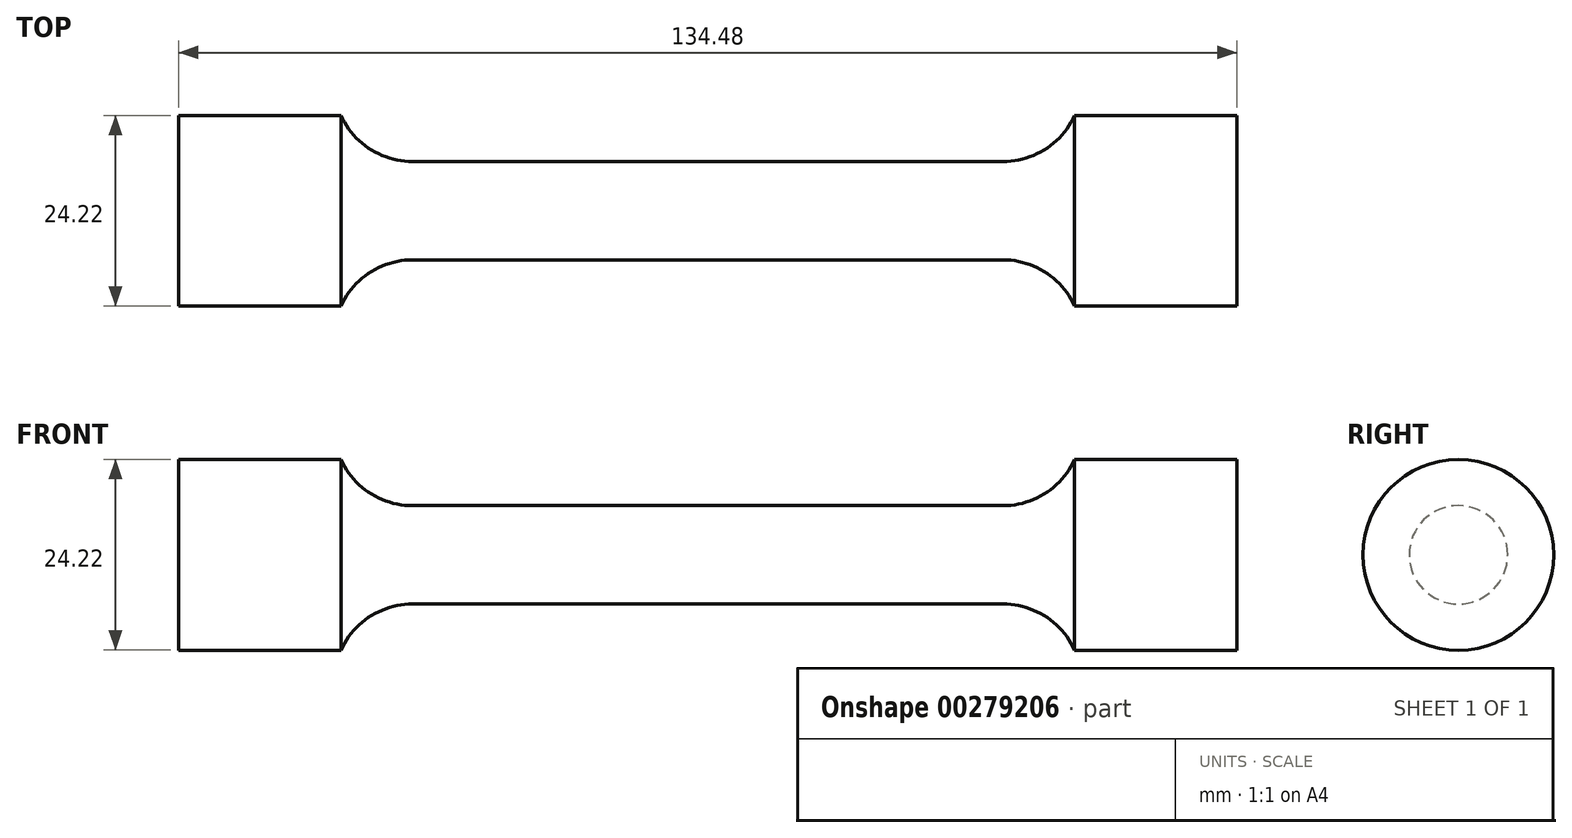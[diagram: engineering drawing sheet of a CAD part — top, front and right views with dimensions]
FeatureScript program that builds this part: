
annotation { "Feature Type Name" : "Feature", "Feature Type Description" : "" }
export const myFeature = defineFeature(function(context is Context, id is Id, definition is map)
    precondition{}
    {
        {
            var Q0;
            Q0=qCreatedBy(makeId("Front.planeOp"),FACE);
            var sketch = newSketch(context, id + "F0", { "sketchPlane" : qUnion([Q0])});
            skLineSegment(sketch, "E0", {"start": v(0, 6.25) * mm, "end": v(37.5, 6.25) * mm});
            skArc(sketch, "E1", {"start": v(37.5, 6.25) * mm, "mid": v(42.91, 7.84) * mm, "end": v(46.6, 12.11) * mm});
            skLineSegment(sketch, "E2", {"start": v(46.6, 12.11) * mm, "end": v(67.24, 12.11) * mm});
            skLineSegment(sketch, "E3", {"start": v(67.24, 12.11) * mm, "end": v(67.24, 0) * mm});
            skLineSegment(sketch, "E4.MirrorCS", {"start": v(0, 6.25) * mm, "end": v(-37.5, 6.25) * mm});
            skLineSegment(sketch, "E5.MirrorCS", {"start": v(-67.24, 12.11) * mm, "end": v(-67.24, 0) * mm});
            skLineSegment(sketch, "E6.MirrorCS", {"start": v(-46.6, 12.11) * mm, "end": v(-67.24, 12.11) * mm});
            skArc(sketch, "E7.MirrorCS", {"start": v(-37.5, 6.25) * mm, "mid": v(-42.91, 7.84) * mm, "end": v(-46.6, 12.11) * mm});
            skLineSegment(sketch, "E8", {"start": v(-67.24, 0) * mm, "end": v(67.24, 0) * mm});
            skSolve(sketch);
        }
        {
            var Q0;
            Q0=makeQuery(id+"F0.imprint","IMPRINT",FACE,{"disambiguationData":[TD([[makeQuery(id+"F0.imprint","IMPRINT",EDGE,{"derivedFrom":sQuery(id+"F0.wireOp",EDGE,"E0")}),-1.0]])]});
            var Q1;
            Q1=sQuery(id+"F0.wireOp",EDGE,"E8");
            revolve(context, id + "F1", {"entities" : qUnion([Q0]), "axis" : qUnion([Q1]), "revolveType" : RevolveType.FULL, "oppositeDirection" : true});
        }
    });
